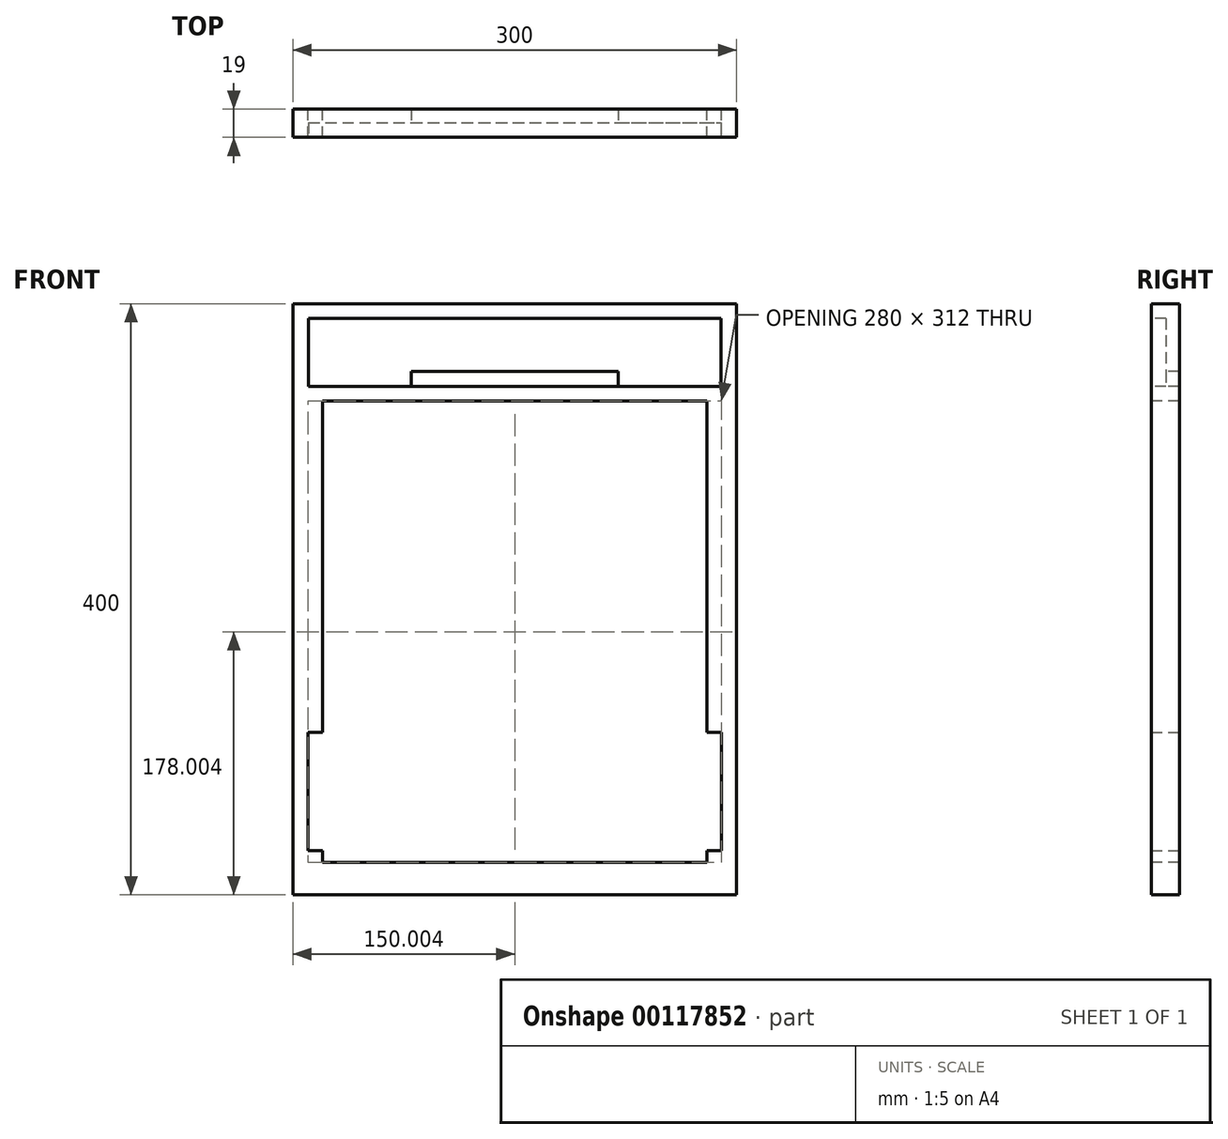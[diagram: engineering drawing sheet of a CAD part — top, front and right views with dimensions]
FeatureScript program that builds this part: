
annotation { "Feature Type Name" : "Feature", "Feature Type Description" : "" }
export const myFeature = defineFeature(function(context is Context, id is Id, definition is map)
    precondition{}
    {
        {
            var Q0;
            Q0=qCreatedBy(makeId("Front.planeOp"),FACE);
            var sketch = newSketch(context, id + "F0", { "sketchPlane" : qUnion([Q0])});
            skLineSegment(sketch, "E0.bottom", {"start": v(-144.68, 130.84) * mm, "end": v(155.32, 130.84) * mm});
            skLineSegment(sketch, "E0.top", {"start": v(-144.68, -269.16) * mm, "end": v(155.32, -269.16) * mm});
            skLineSegment(sketch, "E0.left", {"start": v(-144.68, 130.84) * mm, "end": v(-144.68, -269.16) * mm});
            skLineSegment(sketch, "E0.right", {"start": v(155.32, 130.84) * mm, "end": v(155.32, -269.16) * mm});
            skSolve(sketch);
        }
        {
            var Q0;
            Q0 = qSketchRegion(id + "F0", true);
            extrude(context, id + "F1", {"entities" : qUnion([Q0]), "depth" : 19 * mm});
        }
        {
            var Q0;
            Q0=makeQuery(id+"F1.opExtrude","CAP_FACE",FACE,{"disambiguationData":[OSD([sQuery(id+"F0.wireOp",EDGE,"E0.bottom"),sQuery(id+"F0.wireOp",EDGE,"E0.top"),sQuery(id+"F0.wireOp",EDGE,"E0.left"),sQuery(id+"F0.wireOp",EDGE,"E0.right")])],"isStart":false});
            var sketch = newSketch(context, id + "F2", { "sketchPlane" : qUnion([Q0])});
            skLineSegment(sketch, "E1.bottom", {"start": v(-134.18, 120.84) * mm, "end": v(144.82, 120.84) * mm});
            skLineSegment(sketch, "E1.top", {"start": v(-134.18, 74.84) * mm, "end": v(144.82, 74.84) * mm});
            skLineSegment(sketch, "E1.left", {"start": v(-134.18, 120.84) * mm, "end": v(-134.18, 74.84) * mm});
            skLineSegment(sketch, "E1.right", {"start": v(144.82, 120.84) * mm, "end": v(144.82, 74.84) * mm});
            skSolve(sketch);
        }
        {
            var Q0;
            Q0 = qSketchRegion(id + "F2", true);
            extrude(context, id + "F3", {"entities" : qUnion([Q0]), "operationType" : NewBodyOperationType.REMOVE, "oppositeDirection" : true, "depth" : 10 * mm});
        }
        {
            var Q0;
            Q0=makeQuery(id+"F3.boolean.opBoolean","COPY",FACE,{"derivedFrom":makeQuery(id+"F3.opExtrude","CAP_FACE",FACE,{"disambiguationData":[OSD([sQuery(id+"F2.wireOp",EDGE,"E1.bottom"),sQuery(id+"F2.wireOp",EDGE,"E1.top"),sQuery(id+"F2.wireOp",EDGE,"E1.left"),sQuery(id+"F2.wireOp",EDGE,"E1.right")])],"isStart":false})});
            var sketch = newSketch(context, id + "F4", { "sketchPlane" : qUnion([Q0])});
            skLineSegment(sketch, "E2.bottom", {"start": v(-64.68, 84.84) * mm, "end": v(75.32, 84.84) * mm});
            skLineSegment(sketch, "E2.top", {"start": v(-64.68, 74.84) * mm, "end": v(75.32, 74.84) * mm});
            skLineSegment(sketch, "E2.left", {"start": v(-64.68, 84.84) * mm, "end": v(-64.68, 74.84) * mm});
            skLineSegment(sketch, "E2.right", {"start": v(75.32, 84.84) * mm, "end": v(75.32, 74.84) * mm});
            skSolve(sketch);
        }
        {
            var Q0;
            Q0 = qSketchRegion(id + "F4", true);
            extrude(context, id + "F5", {"entities" : qUnion([Q0]), "operationType" : NewBodyOperationType.REMOVE, "oppositeDirection" : true, "depth" : 10 * mm});
        }
        {
            var Q0;
            Q0=makeQuery(id+"F1.opExtrude","CAP_FACE",FACE,{"disambiguationData":[OSD([sQuery(id+"F0.wireOp",EDGE,"E0.bottom"),sQuery(id+"F0.wireOp",EDGE,"E0.top"),sQuery(id+"F0.wireOp",EDGE,"E0.left"),sQuery(id+"F0.wireOp",EDGE,"E0.right")])],"isStart":false});
            var sketch = newSketch(context, id + "F6", { "sketchPlane" : qUnion([Q0])});
            skLineSegment(sketch, "E3.bottom", {"start": v(-124.68, 64.84) * mm, "end": v(135.32, 64.84) * mm});
            skLineSegment(sketch, "E3.top", {"start": v(-124.68, -247.16) * mm, "end": v(135.32, -247.16) * mm});
            skLineSegment(sketch, "E3.left", {"start": v(-124.68, 64.84) * mm, "end": v(-124.68, -247.16) * mm});
            skLineSegment(sketch, "E3.right", {"start": v(135.32, 64.84) * mm, "end": v(135.32, -247.16) * mm});
            skSolve(sketch);
        }
        {
            var Q0;
            Q0 = qSketchRegion(id + "F6", true);
            extrude(context, id + "F7", {"entities" : qUnion([Q0]), "operationType" : NewBodyOperationType.REMOVE, "oppositeDirection" : true, "depth" : 19 * mm});
        }
        {
            var Q0;
            Q0=makeQuery(id+"F1.opExtrude","CAP_FACE",FACE,{"disambiguationData":[OSD([sQuery(id+"F0.wireOp",EDGE,"E0.bottom"),sQuery(id+"F0.wireOp",EDGE,"E0.top"),sQuery(id+"F0.wireOp",EDGE,"E0.left"),sQuery(id+"F0.wireOp",EDGE,"E0.right")])],"isStart":true});
            var sketch = newSketch(context, id + "F8", { "sketchPlane" : qUnion([Q0])});
            skLineSegment(sketch, "E4.bottom", {"start": v(-135.32, -159.16) * mm, "end": v(-145.32, -159.16) * mm});
            skLineSegment(sketch, "E4.top", {"start": v(-135.32, -239.16) * mm, "end": v(-145.32, -239.16) * mm});
            skLineSegment(sketch, "E4.left", {"start": v(-135.32, -159.16) * mm, "end": v(-135.32, -239.16) * mm});
            skLineSegment(sketch, "E4.right", {"start": v(-145.32, -159.16) * mm, "end": v(-145.32, -239.16) * mm});
            skSolve(sketch);
        }
        {
            var Q0;
            Q0 = qSketchRegion(id + "F8", true);
            extrude(context, id + "F9", {"entities" : qUnion([Q0]), "operationType" : NewBodyOperationType.REMOVE, "oppositeDirection" : true, "depth" : 19 * mm});
        }
        {
            var Q0;
            Q0=makeQuery(id+"F1.opExtrude","CAP_FACE",FACE,{"disambiguationData":[OSD([sQuery(id+"F0.wireOp",EDGE,"E0.bottom"),sQuery(id+"F0.wireOp",EDGE,"E0.top"),sQuery(id+"F0.wireOp",EDGE,"E0.left"),sQuery(id+"F0.wireOp",EDGE,"E0.right")])],"isStart":true});
            var sketch = newSketch(context, id + "F10", { "sketchPlane" : qUnion([Q0])});
            skLineSegment(sketch, "E5.bottom", {"start": v(124.68, -159.16) * mm, "end": v(134.68, -159.16) * mm});
            skLineSegment(sketch, "E5.top", {"start": v(124.68, -239.16) * mm, "end": v(134.68, -239.16) * mm});
            skLineSegment(sketch, "E5.left", {"start": v(124.68, -159.16) * mm, "end": v(124.68, -239.16) * mm});
            skLineSegment(sketch, "E5.right", {"start": v(134.68, -159.16) * mm, "end": v(134.68, -239.16) * mm});
            skSolve(sketch);
        }
        {
            var Q0;
            Q0 = qSketchRegion(id + "F10", true);
            extrude(context, id + "F11", {"entities" : qUnion([Q0]), "operationType" : NewBodyOperationType.REMOVE, "oppositeDirection" : true, "depth" : 19 * mm});
        }
    });
